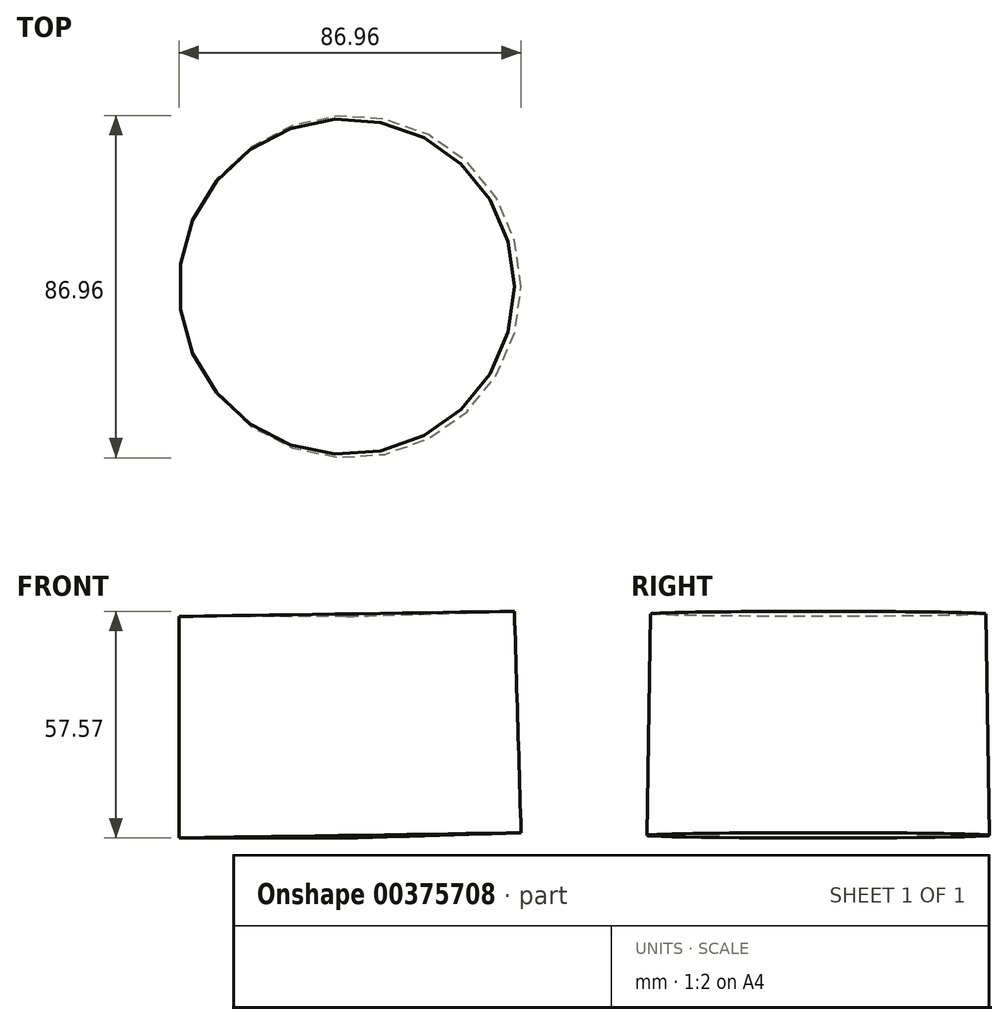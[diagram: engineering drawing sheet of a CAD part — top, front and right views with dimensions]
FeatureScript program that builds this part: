
annotation { "Feature Type Name" : "Feature", "Feature Type Description" : "" }
export const myFeature = defineFeature(function(context is Context, id is Id, definition is map)
    precondition{}
    {
        {
            var Q0;
            Q0=qCreatedBy(makeId("Front.planeOp"),FACE);
            var sketch = newSketch(context, id + "F0", { "sketchPlane" : qUnion([Q0])});
            skLineSegment(sketch, "E0.bottom", {"start": v(-43.49, 27.14) * mm, "end": v(41.78, 27.14) * mm});
            skLineSegment(sketch, "E0.top", {"start": v(-43.49, -29.13) * mm, "end": v(41.78, -29.13) * mm});
            skLineSegment(sketch, "E0.left", {"start": v(-43.49, 27.14) * mm, "end": v(-43.49, -29.13) * mm});
            skLineSegment(sketch, "E0.right", {"start": v(41.78, 27.14) * mm, "end": v(41.78, -29.13) * mm});
            skLineSegment(sketch, "E1", {"start": v(-0.85, 27.14) * mm, "end": v(0, -29.13) * mm});
            skSolve(sketch);
        }
        {
            var Q0;
            {var subQ0=sQuery(id+"F0.wireOp",EDGE,"E0.left");Q0=makeQuery(id+"F0.imprint","IMPRINT",FACE,{"disambiguationData":[TD([[makeQuery(id+"F0.imprint","IMPRINT",EDGE,{"derivedFrom":subQ0}),1.0]])]});}
            var Q1;
            Q1=sQuery(id+"F0.wireOp",EDGE,"E1");
            revolve(context, id + "F1", {"entities" : qUnion([Q0]), "axis" : qUnion([Q1]), "revolveType" : RevolveType.FULL});
        }
    });
